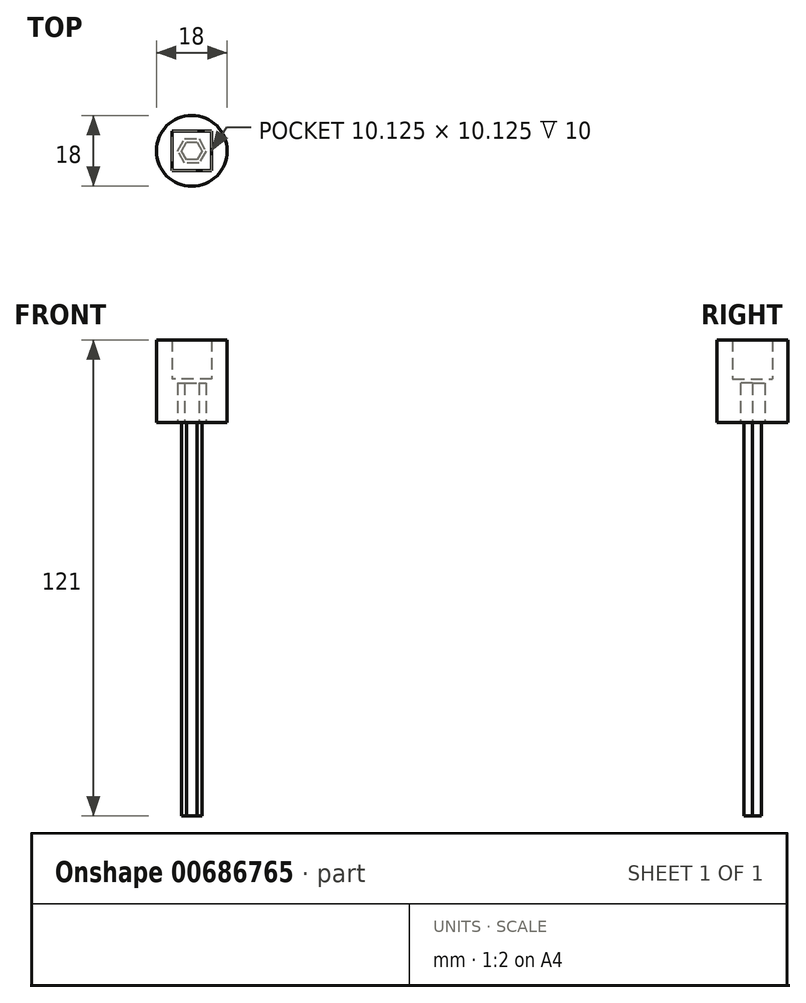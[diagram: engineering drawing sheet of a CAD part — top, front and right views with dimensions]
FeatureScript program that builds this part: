
annotation { "Feature Type Name" : "Feature", "Feature Type Description" : "" }
export const myFeature = defineFeature(function(context is Context, id is Id, definition is map)
    precondition{}
    {
        {
            var Q0;
            Q0=qCreatedBy(makeId("Top.planeOp"),FACE);
            var sketch = newSketch(context, id + "F0", { "sketchPlane" : qUnion([Q0])});
            skCircle(sketch, "E0.cCircle", {"center": v(0, 0) * mm, "radius": 2.5 * mm, "construction": true});
            skLineSegment(sketch, "E0.0", {"start": v(2.89, 0) * mm, "end": v(1.44, -2.5) * mm, "construction": true});
            skLineSegment(sketch, "E0.1", {"start": v(1.44, -2.5) * mm, "end": v(-1.44, -2.5) * mm, "construction": true});
            skLineSegment(sketch, "E0.2", {"start": v(-1.44, -2.5) * mm, "end": v(-2.89, 0) * mm, "construction": true});
            skLineSegment(sketch, "E0.3", {"start": v(-2.89, 0) * mm, "end": v(-1.44, 2.5) * mm, "construction": true});
            skLineSegment(sketch, "E0.4", {"start": v(-1.44, 2.5) * mm, "end": v(1.44, 2.5) * mm, "construction": true});
            skLineSegment(sketch, "E0.5", {"start": v(1.44, 2.5) * mm, "end": v(2.89, 0) * mm, "construction": true});
            skPoint(sketch, "E0.0.midPoint", {"position": v(2.17, -1.25) * mm});
            skLineSegment(sketch, "E1.0", {"start": v(-3.58, 0) * mm, "end": v(-1.79, 3.1) * mm});
            skLineSegment(sketch, "E1.1", {"start": v(1.79, 3.1) * mm, "end": v(3.58, 0) * mm});
            skLineSegment(sketch, "E1.2", {"start": v(3.58, 0) * mm, "end": v(1.79, -3.1) * mm});
            skLineSegment(sketch, "E1.3", {"start": v(-1.79, 3.1) * mm, "end": v(1.79, 3.1) * mm});
            skLineSegment(sketch, "E1.4", {"start": v(1.79, -3.1) * mm, "end": v(-1.79, -3.1) * mm});
            skLineSegment(sketch, "E1.5", {"start": v(-1.79, -3.1) * mm, "end": v(-3.58, 0) * mm});
            skCircle(sketch, "E2", {"center": v(0, 0) * mm, "radius": 9 * mm});
            skSolve(sketch);
        }
        {
            var Q0;
            Q0 = qSketchRegion(id + "F0", true);
            extrude(context, id + "F1", {"entities" : qUnion([Q0]), "depth" : 10 * mm, "offsetDistance" : 25 * mm});
        }
        {
            var Q0;
            Q0=makeQuery(id+"F1.opExtrude","CAP_FACE",FACE,{"disambiguationData":[OSD([sQuery(id+"F0.wireOp",EDGE,"E1.0"),sQuery(id+"F0.wireOp",EDGE,"E1.1"),sQuery(id+"F0.wireOp",EDGE,"E1.2"),sQuery(id+"F0.wireOp",EDGE,"E1.3"),sQuery(id+"F0.wireOp",EDGE,"E1.4"),sQuery(id+"F0.wireOp",EDGE,"E1.5"),sQuery(id+"F0.wireOp",EDGE,"E2")])],"isStart":false});
            var sketch = newSketch(context, id + "F2", { "sketchPlane" : qUnion([Q0])});
            skCircle(sketch, "E3.0", {"center": v(0, 0) * mm, "radius": 9 * mm});
            skSolve(sketch);
        }
        {
            var Q0;
            Q0 = qSketchRegion(id + "F2", true);
            extrude(context, id + "F3", {"entities" : qUnion([Q0]), "operationType" : NewBodyOperationType.ADD, "depth" : 1 * mm, "offsetDistance" : 25 * mm});
        }
        {
            var Q0;
            Q0=makeQuery(id+"F3.opExtrude","CAP_FACE",FACE,{"disambiguationData":[OSD([sQuery(id+"F2.wireOp",EDGE,"E3.0")])],"isStart":false});
            var sketch = newSketch(context, id + "F4", { "sketchPlane" : qUnion([Q0])});
            skLineSegment(sketch, "E4.bottom", {"start": v(5.06, -5.06) * mm, "end": v(-5.06, -5.06) * mm});
            skLineSegment(sketch, "E4.top", {"start": v(5.06, 5.06) * mm, "end": v(-5.06, 5.06) * mm});
            skLineSegment(sketch, "E4.left", {"start": v(5.06, -5.06) * mm, "end": v(5.06, 5.06) * mm});
            skLineSegment(sketch, "E4.right", {"start": v(-5.06, -5.06) * mm, "end": v(-5.06, 5.06) * mm});
            skPoint(sketch, "E4.middle", {"position": v(0, 0) * mm});
            skCircle(sketch, "E5.0", {"center": v(0, 0) * mm, "radius": 9 * mm});
            skSolve(sketch);
        }
        {
            var Q0;
            Q0 = qSketchRegion(id + "F4", true);
            extrude(context, id + "F5", {"entities" : qUnion([Q0]), "operationType" : NewBodyOperationType.ADD, "depth" : 10 * mm, "offsetDistance" : 25 * mm});
        }
        {
            var Q0;
            Q0=makeQuery(id+"F1.opExtrude","CAP_FACE",FACE,{"disambiguationData":[OSD([sQuery(id+"F0.wireOp",EDGE,"E1.0"),sQuery(id+"F0.wireOp",EDGE,"E1.1"),sQuery(id+"F0.wireOp",EDGE,"E1.2"),sQuery(id+"F0.wireOp",EDGE,"E1.3"),sQuery(id+"F0.wireOp",EDGE,"E1.4"),sQuery(id+"F0.wireOp",EDGE,"E1.5"),sQuery(id+"F0.wireOp",EDGE,"E2")])],"isStart":true});
            var sketch = newSketch(context, id + "F6", { "sketchPlane" : qUnion([Q0])});
            skLineSegment(sketch, "E6.0", {"start": v(1.44, 2.5) * mm, "end": v(-1.44, 2.5) * mm, "construction": true});
            skLineSegment(sketch, "E7.0", {"start": v(-1.44, 2.5) * mm, "end": v(-2.89, 0) * mm, "construction": true});
            skLineSegment(sketch, "E8.0", {"start": v(-2.89, 0) * mm, "end": v(-1.44, -2.5) * mm, "construction": true});
            skLineSegment(sketch, "E9.0", {"start": v(-1.44, -2.5) * mm, "end": v(1.44, -2.5) * mm, "construction": true});
            skLineSegment(sketch, "E10.0", {"start": v(1.44, -2.5) * mm, "end": v(2.89, 0) * mm, "construction": true});
            skLineSegment(sketch, "E11.0", {"start": v(2.89, 0) * mm, "end": v(1.44, 2.5) * mm, "construction": true});
            skLineSegment(sketch, "E12.0", {"start": v(-1.3, -2.25) * mm, "end": v(1.3, -2.25) * mm});
            skLineSegment(sketch, "E12.1", {"start": v(2.6, 0) * mm, "end": v(1.3, 2.25) * mm});
            skLineSegment(sketch, "E12.2", {"start": v(1.3, 2.25) * mm, "end": v(-1.3, 2.25) * mm});
            skLineSegment(sketch, "E12.3", {"start": v(1.3, -2.25) * mm, "end": v(2.6, 0) * mm});
            skLineSegment(sketch, "E12.4", {"start": v(-1.3, 2.25) * mm, "end": v(-2.6, 0) * mm});
            skLineSegment(sketch, "E12.5", {"start": v(-2.6, 0) * mm, "end": v(-1.3, -2.25) * mm});
            skSolve(sketch);
        }
        {
            var Q0;
            Q0 = qSketchRegion(id + "F6", true);
            extrude(context, id + "F7", {"entities" : qUnion([Q0]), "depth" : 100 * mm, "offsetDistance" : 25 * mm});
        }
    });
